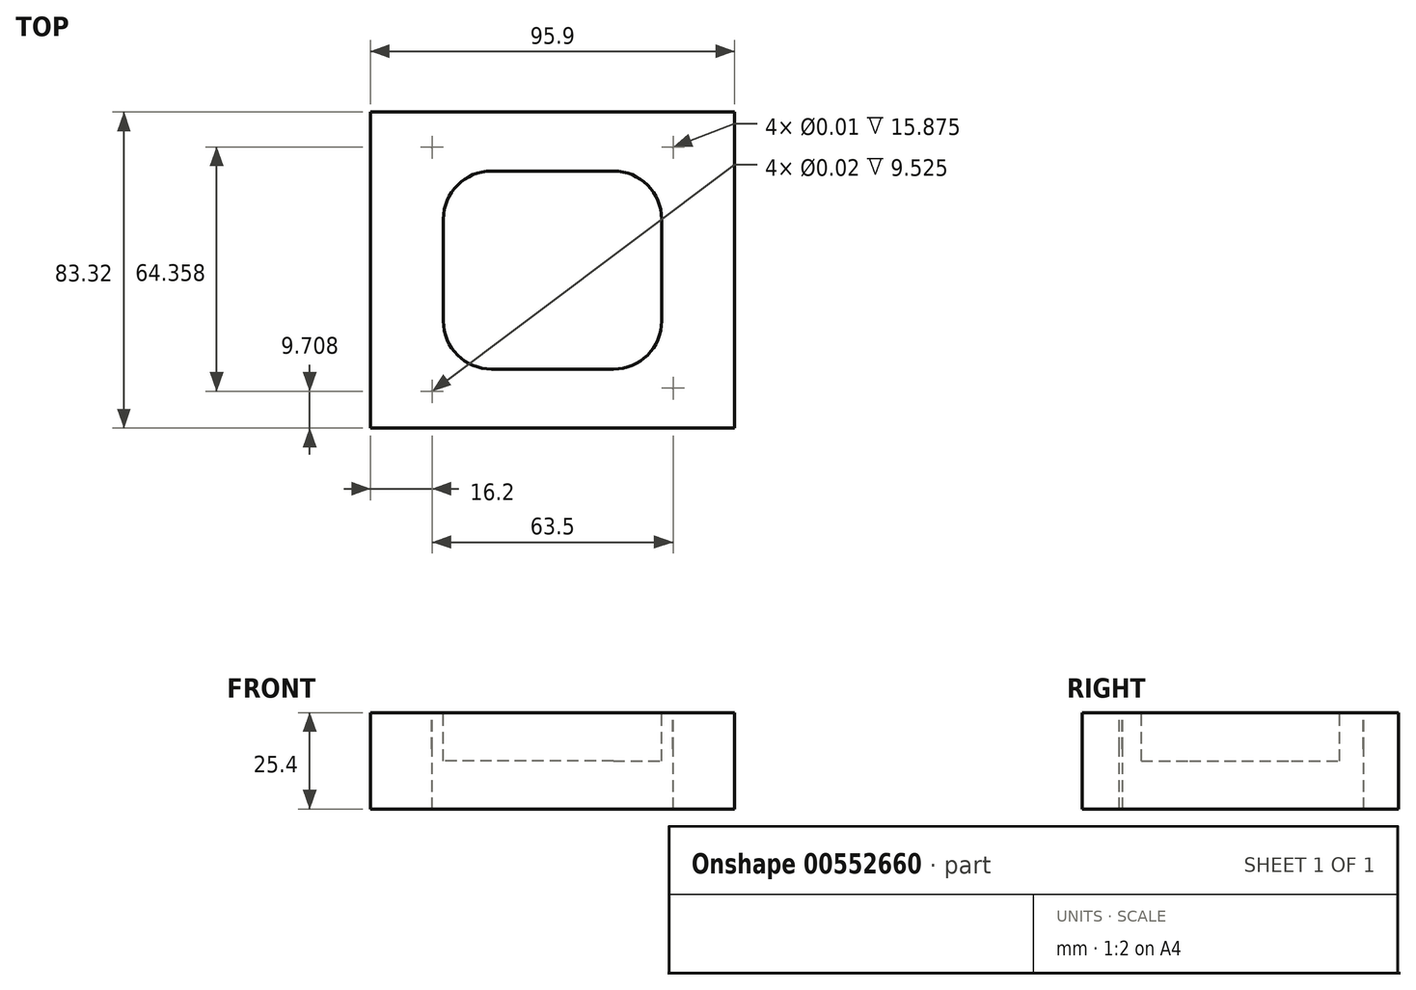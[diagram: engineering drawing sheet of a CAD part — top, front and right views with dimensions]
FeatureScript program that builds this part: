
annotation { "Feature Type Name" : "Feature", "Feature Type Description" : "" }
export const myFeature = defineFeature(function(context is Context, id is Id, definition is map)
    precondition{}
    {
        {
            var Q0;
            Q0=qCreatedBy(makeId("Top.planeOp"),FACE);
            var sketch = newSketch(context, id + "F0", { "sketchPlane" : qUnion([Q0])});
            skLineSegment(sketch, "E0.bottom", {"start": v(47.95, -41.66) * mm, "end": v(-47.95, -41.66) * mm});
            skLineSegment(sketch, "E0.top", {"start": v(47.95, 41.66) * mm, "end": v(-47.95, 41.66) * mm});
            skLineSegment(sketch, "E0.left", {"start": v(47.95, -41.66) * mm, "end": v(47.95, 41.66) * mm});
            skLineSegment(sketch, "E0.right", {"start": v(-47.95, -41.66) * mm, "end": v(-47.95, 41.66) * mm});
            skPoint(sketch, "E0.middle", {"position": v(0, 0) * mm});
            skSolve(sketch);
        }
        {
            var Q0;
            Q0 = qSketchRegion(id + "F0", true);
            extrude(context, id + "F1", {"entities" : qUnion([Q0]), "oppositeDirection" : true, "depth" : 25.4 * mm, "offsetDistance" : 25.4 * mm});
        }
        {
            var Q0;
            Q0=makeQuery(id+"F1.opExtrude","CAP_FACE",FACE,{"disambiguationData":[OSD([sQuery(id+"F0.wireOp",EDGE,"E0.bottom"),sQuery(id+"F0.wireOp",EDGE,"E0.top"),sQuery(id+"F0.wireOp",EDGE,"E0.left"),sQuery(id+"F0.wireOp",EDGE,"E0.right")])],"isStart":true});
            var sketch = newSketch(context, id + "F2", { "sketchPlane" : qUnion([Q0])});
            skLineSegment(sketch, "E1.bottom", {"start": v(28.74, -26.12) * mm, "end": v(-28.74, -26.12) * mm});
            skLineSegment(sketch, "E1.top", {"start": v(28.74, 26.12) * mm, "end": v(-28.74, 26.12) * mm});
            skLineSegment(sketch, "E1.left", {"start": v(28.74, -26.12) * mm, "end": v(28.74, 26.12) * mm});
            skLineSegment(sketch, "E1.right", {"start": v(-28.74, -26.12) * mm, "end": v(-28.74, 26.12) * mm});
            skPoint(sketch, "E1.middle", {"position": v(0, 0) * mm});
            skSolve(sketch);
        }
        {
            var Q0;
            Q0=makeQuery(id+"F2.imprint","IMPRINT",FACE,{"disambiguationData":[TD([[makeQuery(id+"F2.imprint","IMPRINT",EDGE,{"derivedFrom":sQuery(id+"F2.wireOp",EDGE,"E1.bottom")}),-1.0]])]});
            extrude(context, id + "F3", {"entities" : qUnion([Q0]), "operationType" : NewBodyOperationType.REMOVE, "oppositeDirection" : true, "depth" : 12.7 * mm, "offsetDistance" : 25.4 * mm});
        }
        {
            var Q0;
            Q0=makeQuery(id+"F3.boolean.opBoolean","COPY",EDGE,{"derivedFrom":makeQuery(id+"F3.opExtrude","SWEPT_EDGE",EDGE,{"disambiguationData":[OSD([sQuery(id+"F2.wireOp",EDGE,"E1.top"),sQuery(id+"F2.wireOp",EDGE,"E1.right")])]})});
            var Q1;
            Q1=makeQuery(id+"F3.boolean.opBoolean","COPY",EDGE,{"derivedFrom":makeQuery(id+"F3.opExtrude","SWEPT_EDGE",EDGE,{"disambiguationData":[OSD([sQuery(id+"F2.wireOp",EDGE,"E1.top"),sQuery(id+"F2.wireOp",EDGE,"E1.left")])]})});
            var Q2;
            Q2=makeQuery(id+"F3.boolean.opBoolean","COPY",EDGE,{"derivedFrom":makeQuery(id+"F3.opExtrude","SWEPT_EDGE",EDGE,{"disambiguationData":[OSD([sQuery(id+"F2.wireOp",EDGE,"E1.bottom"),sQuery(id+"F2.wireOp",EDGE,"E1.right")])]})});
            var Q3;
            Q3=makeQuery(id+"F3.boolean.opBoolean","COPY",EDGE,{"derivedFrom":makeQuery(id+"F3.opExtrude","SWEPT_EDGE",EDGE,{"disambiguationData":[OSD([sQuery(id+"F2.wireOp",EDGE,"E1.bottom"),sQuery(id+"F2.wireOp",EDGE,"E1.left")])]})});
            fillet(context, id + "F4", {"entities" : qUnion([Q0, Q1, Q2, Q3]), "radius" : 12.7 * mm, "tangentPropagation" : true, "allowEdgeOverflow" : false});
        }
        {
            var Q0;
            Q0=makeQuery(id+"F1.opExtrude","CAP_FACE",FACE,{"disambiguationData":[OSD([sQuery(id+"F0.wireOp",EDGE,"E0.bottom"),sQuery(id+"F0.wireOp",EDGE,"E0.top"),sQuery(id+"F0.wireOp",EDGE,"E0.left"),sQuery(id+"F0.wireOp",EDGE,"E0.right")])],"isStart":true});
            var sketch = newSketch(context, id + "F5", { "sketchPlane" : qUnion([Q0])});
            skPoint(sketch, "E2", {"position": v(-31.75, 32.4) * mm});
            skPoint(sketch, "E3", {"position": v(31.75, 32.4) * mm});
            skPoint(sketch, "E4", {"position": v(31.75, -31.1) * mm});
            skPoint(sketch, "E5", {"position": v(-31.75, -31.95) * mm});
            skSolve(sketch);
        }
        {
            var Q0;
            Q0=sQuery(id+"F5.wireOp",VERTEX,"E2");
            var Q1;
            Q1=sQuery(id+"F5.wireOp",VERTEX,"E3");
            var Q2;
            Q2=sQuery(id+"F5.wireOp",VERTEX,"E4");
            var Q3;
            Q3=sQuery(id+"F5.wireOp",VERTEX,"E5");
            var Q4;
            Q4=makeQuery(id+"F1.opExtrude","SWEPT_BODY",BODY,{"disambiguationData":[OSD([sQuery(id+"F0.wireOp",EDGE,"E0.bottom"),sQuery(id+"F0.wireOp",EDGE,"E0.top"),sQuery(id+"F0.wireOp",EDGE,"E0.left"),sQuery(id+"F0.wireOp",EDGE,"E0.right")])]});
            hole(context, id + "F6", {"style" : HoleStyle.C_BORE, "endStyle" : HoleEndStyle.THROUGH, "standardTappedOrClearance" : lookupTablePath({ "standard" : "ANSI", "size" : "3/8 (0.38)", "type" : "Drilled" }), "standardBlindInLast" : lookupTablePath({ "standard" : "ANSI", "size" : "3/8", "type" : "Drilled" }), "holeDiameter" : 3 / 203.2 * mm, "cBoreDiameter" : 5 / 203.2 * mm, "cBoreDepth" : 9.52 * mm, "majorDiameter" : 9.52 * mm, "tappedDepth" : 12.7 * mm, "tapClearance" : 3, "locations" : qUnion([Q0, Q1, Q2, Q3]), "scope" : qUnion([Q4])});
        }
    });
